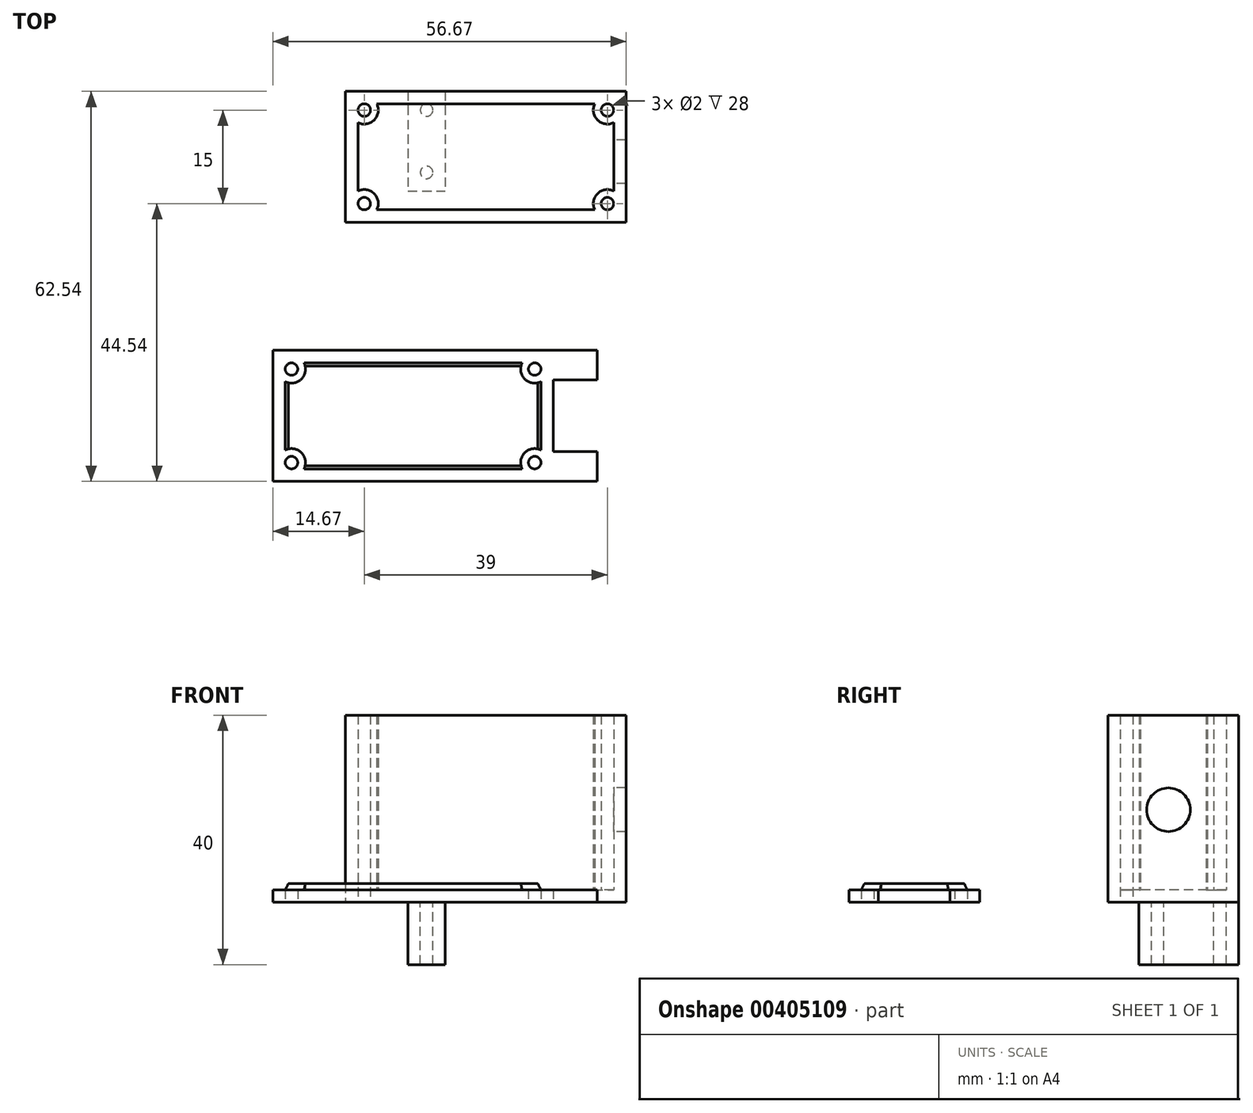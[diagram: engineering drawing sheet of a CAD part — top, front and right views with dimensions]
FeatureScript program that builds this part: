
annotation { "Feature Type Name" : "Feature", "Feature Type Description" : "" }
export const myFeature = defineFeature(function(context is Context, id is Id, definition is map)
    precondition{}
    {
        {
            var Q0;
            Q0=qCreatedBy(makeId("Top.planeOp"),FACE);
            var sketch = newSketch(context, id + "F0", { "sketchPlane" : qUnion([Q0])});
            skCircle(sketch, "E0", {"center": v(0, 0) * mm, "radius": 1 * mm});
            skCircle(sketch, "E1", {"center": v(0, -10) * mm, "radius": 1 * mm});
            skLineSegment(sketch, "E2.bottom", {"start": v(-3, 3) * mm, "end": v(3, 3) * mm});
            skLineSegment(sketch, "E2.top", {"start": v(-3, -13) * mm, "end": v(3, -13) * mm});
            skLineSegment(sketch, "E2.left", {"start": v(-3, 3) * mm, "end": v(-3, -13) * mm});
            skLineSegment(sketch, "E2.right", {"start": v(3, 3) * mm, "end": v(3, -13) * mm});
            skLineSegment(sketch, "E3.bottom", {"start": v(-13, 3) * mm, "end": v(32, 3) * mm});
            skLineSegment(sketch, "E3.top", {"start": v(-13, -18) * mm, "end": v(32, -18) * mm});
            skLineSegment(sketch, "E3.left", {"start": v(-13, 3) * mm, "end": v(-13, -18) * mm});
            skLineSegment(sketch, "E3.right", {"start": v(32, 3) * mm, "end": v(32, -18) * mm});
            skLineSegment(sketch, "E4.bottom", {"start": v(-11, 1) * mm, "end": v(30, 1) * mm});
            skLineSegment(sketch, "E4.top", {"start": v(-11, -16) * mm, "end": v(30, -16) * mm});
            skLineSegment(sketch, "E4.left", {"start": v(-11, 1) * mm, "end": v(-11, -16) * mm});
            skLineSegment(sketch, "E4.right", {"start": v(30, 1) * mm, "end": v(30, -16) * mm});
            skCircle(sketch, "E5", {"center": v(-10, 0) * mm, "radius": 1 * mm});
            skCircle(sketch, "E6", {"center": v(-10, -15) * mm, "radius": 1 * mm});
            skCircle(sketch, "E7", {"center": v(29, -15) * mm, "radius": 1 * mm});
            skCircle(sketch, "E8", {"center": v(29, 0) * mm, "radius": 1 * mm});
            skCircle(sketch, "E9", {"center": v(-10, 0) * mm, "radius": 2.25 * mm});
            skCircle(sketch, "E10", {"center": v(-10, -15) * mm, "radius": 2.25 * mm});
            skCircle(sketch, "E11", {"center": v(29, 0) * mm, "radius": 2.25 * mm});
            skCircle(sketch, "E12", {"center": v(29, -15) * mm, "radius": 2.25 * mm});
            skCircle(sketch, "E13", {"center": v(-11.67, -41.54) * mm, "radius": 1 * mm});
            skCircle(sketch, "E14", {"center": v(-11.67, -51.54) * mm, "radius": 1 * mm});
            skLineSegment(sketch, "E15.bottom", {"start": v(-14.67, -38.54) * mm, "end": v(-8.67, -38.54) * mm});
            skLineSegment(sketch, "E15.top", {"start": v(-14.67, -54.54) * mm, "end": v(-8.67, -54.54) * mm});
            skLineSegment(sketch, "E15.left", {"start": v(-14.67, -38.54) * mm, "end": v(-14.67, -54.54) * mm});
            skLineSegment(sketch, "E15.right", {"start": v(-8.67, -38.54) * mm, "end": v(-8.67, -54.54) * mm});
            skLineSegment(sketch, "E16.bottom", {"start": v(-24.67, -38.54) * mm, "end": v(20.33, -38.54) * mm});
            skLineSegment(sketch, "E16.top", {"start": v(-24.67, -59.54) * mm, "end": v(20.33, -59.54) * mm});
            skLineSegment(sketch, "E16.left", {"start": v(-24.67, -38.54) * mm, "end": v(-24.67, -59.54) * mm});
            skLineSegment(sketch, "E16.right", {"start": v(20.33, -38.54) * mm, "end": v(20.33, -59.54) * mm});
            skLineSegment(sketch, "E17.bottom", {"start": v(-22.67, -40.54) * mm, "end": v(18.33, -40.54) * mm});
            skLineSegment(sketch, "E17.top", {"start": v(-22.67, -57.54) * mm, "end": v(18.33, -57.54) * mm});
            skLineSegment(sketch, "E17.left", {"start": v(-22.67, -40.54) * mm, "end": v(-22.67, -57.54) * mm});
            skLineSegment(sketch, "E17.right", {"start": v(18.33, -40.54) * mm, "end": v(18.33, -57.54) * mm});
            skCircle(sketch, "E18", {"center": v(-21.67, -41.54) * mm, "radius": 1 * mm});
            skCircle(sketch, "E19", {"center": v(-21.67, -56.54) * mm, "radius": 1 * mm});
            skCircle(sketch, "E20", {"center": v(17.33, -56.54) * mm, "radius": 1 * mm});
            skCircle(sketch, "E21", {"center": v(17.33, -41.54) * mm, "radius": 1 * mm});
            skCircle(sketch, "E22", {"center": v(-21.67, -41.54) * mm, "radius": 2.25 * mm});
            skCircle(sketch, "E23", {"center": v(-21.67, -56.54) * mm, "radius": 2.25 * mm});
            skCircle(sketch, "E24", {"center": v(17.33, -41.54) * mm, "radius": 2.25 * mm});
            skCircle(sketch, "E25", {"center": v(17.33, -56.54) * mm, "radius": 2.25 * mm});
            skLineSegment(sketch, "E26.bottom", {"start": v(20.33, -38.54) * mm, "end": v(27.33, -38.54) * mm});
            skLineSegment(sketch, "E26.top", {"start": v(20.33, -59.54) * mm, "end": v(27.33, -59.54) * mm});
            skLineSegment(sketch, "E26.right", {"start": v(27.33, -38.54) * mm, "end": v(27.33, -59.54) * mm});
            skLineSegment(sketch, "E27", {"start": v(20.33, -54.8) * mm, "end": v(27.33, -54.8) * mm});
            skLineSegment(sketch, "E28", {"start": v(20.33, -43.3) * mm, "end": v(27.33, -43.3) * mm});
            skSolve(sketch);
        }
        {
            var Q0;
            {var subQ2=sQuery(id+"F0.wireOp",EDGE,"E2.left");var subQ4=sQuery(id+"F0.wireOp",EDGE,"E3.bottom");var subQ8=makeQuery(id+"F0.imprint","INTERSECT",VERTEX,{"derivedFrom":[subQ2,subQ4]});Q0=makeQuery(id+"F0.imprint","IMPRINT",FACE,{"disambiguationData":[TD([[makeQuery(id+"F0.imprint","IMPRINT",EDGE,{"disambiguationData":[TD([[subQ8,-1.0]])],"derivedFrom":subQ2}),1.0]])]});}
            var Q1;
            Q1=makeQuery(id+"F0.imprint","IMPRINT",FACE,{"disambiguationData":[TD([[makeQuery(id+"F0.imprint","IMPRINT",EDGE,{"derivedFrom":sQuery(id+"F0.wireOp",EDGE,"E3.top")}),1.0]])]});
            var Q2;
            {var subQ0=sQuery(id+"F0.wireOp",EDGE,"E5");var subQ1=sQuery(id+"F0.wireOp",EDGE,"E4.bottom");var subQ2=makeQuery(id+"F0.imprint","INTERSECT",VERTEX,{"derivedFrom":[subQ1,subQ0]});Q2=makeQuery(id+"F0.imprint","IMPRINT",FACE,{"disambiguationData":[TD([[makeQuery(id+"F0.imprint","IMPRINT",EDGE,{"disambiguationData":[TD([[subQ2,-1.0]])],"derivedFrom":subQ1}),-1.0]])]});}
            var Q3;
            {var subQ1=sQuery(id+"F0.wireOp",EDGE,"E4.left");var subQ5=sQuery(id+"F0.wireOp",EDGE,"E4.bottom");var subQ6=makeQuery(id+"F0.imprint","INTERSECT",VERTEX,{"derivedFrom":[subQ5,subQ1]});Q3=makeQuery(id+"F0.imprint","IMPRINT",FACE,{"disambiguationData":[TD([[makeQuery(id+"F0.imprint","IMPRINT",EDGE,{"disambiguationData":[TD([[subQ6,-1.0]])],"derivedFrom":subQ5}),1.0]])]});}
            var Q4;
            {var subQ3=sQuery(id+"F0.wireOp",EDGE,"E11");var subQ5=sQuery(id+"F0.wireOp",EDGE,"E4.bottom");var subQ8=makeQuery(id+"F0.imprint","INTERSECT",VERTEX,{"derivedFrom":[subQ5,subQ3]});Q4=makeQuery(id+"F0.imprint","IMPRINT",FACE,{"disambiguationData":[TD([[makeQuery(id+"F0.imprint","IMPRINT",EDGE,{"disambiguationData":[TD([[subQ8,-1.0]])],"derivedFrom":subQ5}),1.0]])]});}
            var Q5;
            {var subQ0=sQuery(id+"F0.wireOp",EDGE,"E11");var subQ1=sQuery(id+"F0.wireOp",EDGE,"E4.bottom");var subQ2=makeQuery(id+"F0.imprint","INTERSECT",VERTEX,{"derivedFrom":[subQ1,subQ0]});Q5=makeQuery(id+"F0.imprint","IMPRINT",FACE,{"disambiguationData":[TD([[makeQuery(id+"F0.imprint","IMPRINT",EDGE,{"disambiguationData":[TD([[subQ2,-1.0]])],"derivedFrom":subQ1}),-1.0]])]});}
            var Q6;
            {var subQ0=sQuery(id+"F0.wireOp",EDGE,"E4.right");var subQ1=sQuery(id+"F0.wireOp",EDGE,"E4.bottom");var subQ2=makeQuery(id+"F0.imprint","INTERSECT",VERTEX,{"derivedFrom":[subQ1,subQ0]});Q6=makeQuery(id+"F0.imprint","IMPRINT",FACE,{"disambiguationData":[TD([[makeQuery(id+"F0.imprint","IMPRINT",EDGE,{"disambiguationData":[TD([[subQ2,1.0]])],"derivedFrom":subQ1}),-1.0]])]});}
            var Q7;
            {var subQ0=sQuery(id+"F0.wireOp",EDGE,"E4.left");var subQ1=sQuery(id+"F0.wireOp",EDGE,"E4.bottom");var subQ2=makeQuery(id+"F0.imprint","INTERSECT",VERTEX,{"derivedFrom":[subQ1,subQ0]});Q7=makeQuery(id+"F0.imprint","IMPRINT",FACE,{"disambiguationData":[TD([[makeQuery(id+"F0.imprint","IMPRINT",EDGE,{"disambiguationData":[TD([[subQ2,-1.0]])],"derivedFrom":subQ1}),-1.0]])]});}
            var Q8;
            {var subQ0=sQuery(id+"F0.wireOp",EDGE,"E4.left");var subQ1=sQuery(id+"F0.wireOp",EDGE,"E4.top");var subQ2=makeQuery(id+"F0.imprint","INTERSECT",VERTEX,{"derivedFrom":[subQ1,subQ0]});Q8=makeQuery(id+"F0.imprint","IMPRINT",FACE,{"disambiguationData":[TD([[makeQuery(id+"F0.imprint","IMPRINT",EDGE,{"disambiguationData":[TD([[subQ2,-1.0]])],"derivedFrom":subQ1}),1.0]])]});}
            var Q9;
            {var subQ1=sQuery(id+"F0.wireOp",EDGE,"E4.left");var subQ5=sQuery(id+"F0.wireOp",EDGE,"E4.top");var subQ8=makeQuery(id+"F0.imprint","INTERSECT",VERTEX,{"derivedFrom":[subQ5,subQ1]});Q9=makeQuery(id+"F0.imprint","IMPRINT",FACE,{"disambiguationData":[TD([[makeQuery(id+"F0.imprint","IMPRINT",EDGE,{"disambiguationData":[TD([[subQ8,-1.0]])],"derivedFrom":subQ5}),-1.0]])]});}
            var Q10;
            {var subQ0=sQuery(id+"F0.wireOp",EDGE,"E6");var subQ1=sQuery(id+"F0.wireOp",EDGE,"E4.top");var subQ2=makeQuery(id+"F0.imprint","INTERSECT",VERTEX,{"derivedFrom":[subQ1,subQ0]});Q10=makeQuery(id+"F0.imprint","IMPRINT",FACE,{"disambiguationData":[TD([[makeQuery(id+"F0.imprint","IMPRINT",EDGE,{"disambiguationData":[TD([[subQ2,-1.0]])],"derivedFrom":subQ1}),1.0]])]});}
            var Q11;
            {var subQ0=sQuery(id+"F0.wireOp",EDGE,"E4.right");var subQ1=sQuery(id+"F0.wireOp",EDGE,"E4.top");var subQ2=makeQuery(id+"F0.imprint","INTERSECT",VERTEX,{"derivedFrom":[subQ1,subQ0]});Q11=makeQuery(id+"F0.imprint","IMPRINT",FACE,{"disambiguationData":[TD([[makeQuery(id+"F0.imprint","IMPRINT",EDGE,{"disambiguationData":[TD([[subQ2,1.0]])],"derivedFrom":subQ1}),1.0]])]});}
            var Q12;
            {var subQ0=sQuery(id+"F0.wireOp",EDGE,"E12");var subQ1=sQuery(id+"F0.wireOp",EDGE,"E4.top");var subQ2=makeQuery(id+"F0.imprint","INTERSECT",VERTEX,{"derivedFrom":[subQ1,subQ0]});Q12=makeQuery(id+"F0.imprint","IMPRINT",FACE,{"disambiguationData":[TD([[makeQuery(id+"F0.imprint","IMPRINT",EDGE,{"disambiguationData":[TD([[subQ2,-1.0]])],"derivedFrom":subQ1}),1.0]])]});}
            var Q13;
            {var subQ1=sQuery(id+"F0.wireOp",EDGE,"E4.top");var subQ6=sQuery(id+"F0.wireOp",EDGE,"E12");var subQ8=makeQuery(id+"F0.imprint","INTERSECT",VERTEX,{"derivedFrom":[subQ1,subQ6]});Q13=makeQuery(id+"F0.imprint","IMPRINT",FACE,{"disambiguationData":[TD([[makeQuery(id+"F0.imprint","IMPRINT",EDGE,{"disambiguationData":[TD([[subQ8,-1.0]])],"derivedFrom":subQ1}),-1.0]])]});}
            extrude(context, id + "F1", {"entities" : qUnion([Q0, Q1, Q2, Q3, Q4, Q5, Q6, Q7, Q8, Q9, Q10, Q11, Q12, Q13]), "depth" : 30 * mm});
        }
        {
            var Q0;
            {var subQ18=sQuery(id+"F0.wireOp",EDGE,"E2.top");Q0=makeQuery(id+"F0.imprint","IMPRINT",FACE,{"disambiguationData":[TD([[makeQuery(id+"F0.imprint","IMPRINT",EDGE,{"derivedFrom":subQ18}),-1.0]])]});}
            var Q1;
            Q1=makeQuery(id+"F0.imprint","IMPRINT",FACE,{"disambiguationData":[TD([[makeQuery(id+"F0.imprint","IMPRINT",EDGE,{"derivedFrom":sQuery(id+"F0.wireOp",EDGE,"E0")}),1.0]])]});
            var Q2;
            Q2=makeQuery(id+"F0.imprint","IMPRINT",FACE,{"disambiguationData":[TD([[makeQuery(id+"F0.imprint","IMPRINT",EDGE,{"derivedFrom":sQuery(id+"F0.wireOp",EDGE,"E1")}),1.0]])]});
            var Q3;
            {var subQ4=sQuery(id+"F0.wireOp",EDGE,"E0");Q3=makeQuery(id+"F0.imprint","IMPRINT",FACE,{"disambiguationData":[TD([[makeQuery(id+"F0.imprint","IMPRINT",EDGE,{"derivedFrom":subQ4}),-1.0]])]});}
            var Q4;
            {var subQ0=sQuery(id+"F0.wireOp",EDGE,"E6");var subQ1=sQuery(id+"F0.wireOp",EDGE,"E4.left");var subQ2=makeQuery(id+"F0.imprint","INTERSECT",VERTEX,{"disambiguationData":[OD(0.0)],"derivedFrom":[subQ1,subQ0]});Q4=makeQuery(id+"F0.imprint","IMPRINT",FACE,{"disambiguationData":[TD([[makeQuery(id+"F0.imprint","IMPRINT",EDGE,{"disambiguationData":[TD([[subQ2,-1.0]])],"derivedFrom":subQ1}),1.0]])]});}
            var Q5;
            {var subQ0=sQuery(id+"F0.wireOp",EDGE,"E5");var subQ1=makeQuery(id+"F0.imprint","INTERSECT",VERTEX,{"derivedFrom":[sQuery(id+"F0.wireOp",EDGE,"E4.bottom"),subQ0]});Q5=makeQuery(id+"F0.imprint","IMPRINT",FACE,{"disambiguationData":[TD([[makeQuery(id+"F0.imprint","IMPRINT",EDGE,{"disambiguationData":[TD([[subQ1,-1.0]])],"derivedFrom":subQ0}),1.0]])]});}
            var Q6;
            {var subQ0=sQuery(id+"F0.wireOp",EDGE,"E7");var subQ1=makeQuery(id+"F0.imprint","INTERSECT",VERTEX,{"derivedFrom":[sQuery(id+"F0.wireOp",EDGE,"E4.top"),subQ0]});Q6=makeQuery(id+"F0.imprint","IMPRINT",FACE,{"disambiguationData":[TD([[makeQuery(id+"F0.imprint","IMPRINT",EDGE,{"disambiguationData":[TD([[subQ1,1.0]])],"derivedFrom":subQ0}),1.0]])]});}
            var Q7;
            {var subQ0=sQuery(id+"F0.wireOp",EDGE,"E8");var subQ1=makeQuery(id+"F0.imprint","INTERSECT",VERTEX,{"derivedFrom":[sQuery(id+"F0.wireOp",EDGE,"E4.bottom"),subQ0]});Q7=makeQuery(id+"F0.imprint","IMPRINT",FACE,{"disambiguationData":[TD([[makeQuery(id+"F0.imprint","IMPRINT",EDGE,{"disambiguationData":[TD([[subQ1,1.0]])],"derivedFrom":subQ0}),1.0]])]});}
            extrude(context, id + "F2", {"entities" : qUnion([Q0, Q1, Q2, Q3, Q4, Q5, Q6, Q7]), "operationType" : NewBodyOperationType.ADD, "depth" : 2 * mm});
        }
        {
            var Q0;
            {var subQ4=sQuery(id+"F0.wireOp",EDGE,"E0");Q0=makeQuery(id+"F0.imprint","IMPRINT",FACE,{"disambiguationData":[TD([[makeQuery(id+"F0.imprint","IMPRINT",EDGE,{"derivedFrom":subQ4}),-1.0]])]});}
            var Q1;
            {var subQ2=sQuery(id+"F0.wireOp",EDGE,"E2.left");var subQ4=sQuery(id+"F0.wireOp",EDGE,"E3.bottom");var subQ8=makeQuery(id+"F0.imprint","INTERSECT",VERTEX,{"derivedFrom":[subQ2,subQ4]});Q1=makeQuery(id+"F0.imprint","IMPRINT",FACE,{"disambiguationData":[TD([[makeQuery(id+"F0.imprint","IMPRINT",EDGE,{"disambiguationData":[TD([[subQ8,-1.0]])],"derivedFrom":subQ2}),1.0]])]});}
            extrude(context, id + "F3", {"entities" : qUnion([Q0, Q1]), "operationType" : NewBodyOperationType.ADD, "oppositeDirection" : true, "depth" : 10 * mm});
        }
        {
            var Q0;
            Q0=makeQuery(id+"F0.imprint","IMPRINT",FACE,{"disambiguationData":[TD([[makeQuery(id+"F0.imprint","IMPRINT",EDGE,{"derivedFrom":sQuery(id+"F0.wireOp",EDGE,"E16.top")}),1.0]])]});
            var Q1;
            {var subQ2=sQuery(id+"F0.wireOp",EDGE,"E15.left");var subQ4=sQuery(id+"F0.wireOp",EDGE,"E16.bottom");var subQ8=makeQuery(id+"F0.imprint","INTERSECT",VERTEX,{"derivedFrom":[subQ2,subQ4]});Q1=makeQuery(id+"F0.imprint","IMPRINT",FACE,{"disambiguationData":[TD([[makeQuery(id+"F0.imprint","IMPRINT",EDGE,{"disambiguationData":[TD([[subQ8,-1.0]])],"derivedFrom":subQ2}),1.0]])]});}
            var Q2;
            {var subQ0=sQuery(id+"F0.wireOp",EDGE,"E18");var subQ1=sQuery(id+"F0.wireOp",EDGE,"E17.bottom");var subQ2=makeQuery(id+"F0.imprint","INTERSECT",VERTEX,{"derivedFrom":[subQ1,subQ0]});Q2=makeQuery(id+"F0.imprint","IMPRINT",FACE,{"disambiguationData":[TD([[makeQuery(id+"F0.imprint","IMPRINT",EDGE,{"disambiguationData":[TD([[subQ2,-1.0]])],"derivedFrom":subQ1}),-1.0]])]});}
            var Q3;
            {var subQ0=sQuery(id+"F0.wireOp",EDGE,"E19");var subQ1=sQuery(id+"F0.wireOp",EDGE,"E17.top");var subQ2=makeQuery(id+"F0.imprint","INTERSECT",VERTEX,{"derivedFrom":[subQ1,subQ0]});Q3=makeQuery(id+"F0.imprint","IMPRINT",FACE,{"disambiguationData":[TD([[makeQuery(id+"F0.imprint","IMPRINT",EDGE,{"disambiguationData":[TD([[subQ2,-1.0]])],"derivedFrom":subQ1}),1.0]])]});}
            var Q4;
            {var subQ3=sQuery(id+"F0.wireOp",EDGE,"E24");var subQ5=sQuery(id+"F0.wireOp",EDGE,"E17.bottom");var subQ8=makeQuery(id+"F0.imprint","INTERSECT",VERTEX,{"derivedFrom":[subQ5,subQ3]});Q4=makeQuery(id+"F0.imprint","IMPRINT",FACE,{"disambiguationData":[TD([[makeQuery(id+"F0.imprint","IMPRINT",EDGE,{"disambiguationData":[TD([[subQ8,-1.0]])],"derivedFrom":subQ5}),1.0]])]});}
            var Q5;
            {var subQ0=sQuery(id+"F0.wireOp",EDGE,"E24");var subQ1=sQuery(id+"F0.wireOp",EDGE,"E17.bottom");var subQ2=makeQuery(id+"F0.imprint","INTERSECT",VERTEX,{"derivedFrom":[subQ1,subQ0]});Q5=makeQuery(id+"F0.imprint","IMPRINT",FACE,{"disambiguationData":[TD([[makeQuery(id+"F0.imprint","IMPRINT",EDGE,{"disambiguationData":[TD([[subQ2,-1.0]])],"derivedFrom":subQ1}),-1.0]])]});}
            var Q6;
            {var subQ0=sQuery(id+"F0.wireOp",EDGE,"E25");var subQ1=sQuery(id+"F0.wireOp",EDGE,"E17.top");var subQ2=makeQuery(id+"F0.imprint","INTERSECT",VERTEX,{"derivedFrom":[subQ1,subQ0]});Q6=makeQuery(id+"F0.imprint","IMPRINT",FACE,{"disambiguationData":[TD([[makeQuery(id+"F0.imprint","IMPRINT",EDGE,{"disambiguationData":[TD([[subQ2,-1.0]])],"derivedFrom":subQ1}),1.0]])]});}
            var Q7;
            {var subQ0=sQuery(id+"F0.wireOp",EDGE,"E17.right");var subQ1=sQuery(id+"F0.wireOp",EDGE,"E17.top");var subQ2=makeQuery(id+"F0.imprint","INTERSECT",VERTEX,{"derivedFrom":[subQ1,subQ0]});Q7=makeQuery(id+"F0.imprint","IMPRINT",FACE,{"disambiguationData":[TD([[makeQuery(id+"F0.imprint","IMPRINT",EDGE,{"disambiguationData":[TD([[subQ2,1.0]])],"derivedFrom":subQ1}),1.0]])]});}
            var Q8;
            {var subQ1=sQuery(id+"F0.wireOp",EDGE,"E17.top");var subQ6=sQuery(id+"F0.wireOp",EDGE,"E25");var subQ8=makeQuery(id+"F0.imprint","INTERSECT",VERTEX,{"derivedFrom":[subQ1,subQ6]});Q8=makeQuery(id+"F0.imprint","IMPRINT",FACE,{"disambiguationData":[TD([[makeQuery(id+"F0.imprint","IMPRINT",EDGE,{"disambiguationData":[TD([[subQ8,-1.0]])],"derivedFrom":subQ1}),-1.0]])]});}
            var Q9;
            {var subQ1=sQuery(id+"F0.wireOp",EDGE,"E17.left");var subQ5=sQuery(id+"F0.wireOp",EDGE,"E17.top");var subQ8=makeQuery(id+"F0.imprint","INTERSECT",VERTEX,{"derivedFrom":[subQ5,subQ1]});Q9=makeQuery(id+"F0.imprint","IMPRINT",FACE,{"disambiguationData":[TD([[makeQuery(id+"F0.imprint","IMPRINT",EDGE,{"disambiguationData":[TD([[subQ8,-1.0]])],"derivedFrom":subQ5}),-1.0]])]});}
            var Q10;
            {var subQ1=sQuery(id+"F0.wireOp",EDGE,"E17.left");var subQ5=sQuery(id+"F0.wireOp",EDGE,"E17.bottom");var subQ6=makeQuery(id+"F0.imprint","INTERSECT",VERTEX,{"derivedFrom":[subQ5,subQ1]});Q10=makeQuery(id+"F0.imprint","IMPRINT",FACE,{"disambiguationData":[TD([[makeQuery(id+"F0.imprint","IMPRINT",EDGE,{"disambiguationData":[TD([[subQ6,-1.0]])],"derivedFrom":subQ5}),1.0]])]});}
            var Q11;
            {var subQ0=sQuery(id+"F0.wireOp",EDGE,"E17.left");var subQ1=sQuery(id+"F0.wireOp",EDGE,"E17.bottom");var subQ2=makeQuery(id+"F0.imprint","INTERSECT",VERTEX,{"derivedFrom":[subQ1,subQ0]});Q11=makeQuery(id+"F0.imprint","IMPRINT",FACE,{"disambiguationData":[TD([[makeQuery(id+"F0.imprint","IMPRINT",EDGE,{"disambiguationData":[TD([[subQ2,-1.0]])],"derivedFrom":subQ1}),-1.0]])]});}
            var Q12;
            {var subQ0=sQuery(id+"F0.wireOp",EDGE,"E17.left");var subQ1=sQuery(id+"F0.wireOp",EDGE,"E17.top");var subQ2=makeQuery(id+"F0.imprint","INTERSECT",VERTEX,{"derivedFrom":[subQ1,subQ0]});Q12=makeQuery(id+"F0.imprint","IMPRINT",FACE,{"disambiguationData":[TD([[makeQuery(id+"F0.imprint","IMPRINT",EDGE,{"disambiguationData":[TD([[subQ2,-1.0]])],"derivedFrom":subQ1}),1.0]])]});}
            var Q13;
            {var subQ0=sQuery(id+"F0.wireOp",EDGE,"E17.right");var subQ1=sQuery(id+"F0.wireOp",EDGE,"E17.bottom");var subQ2=makeQuery(id+"F0.imprint","INTERSECT",VERTEX,{"derivedFrom":[subQ1,subQ0]});Q13=makeQuery(id+"F0.imprint","IMPRINT",FACE,{"disambiguationData":[TD([[makeQuery(id+"F0.imprint","IMPRINT",EDGE,{"disambiguationData":[TD([[subQ2,1.0]])],"derivedFrom":subQ1}),-1.0]])]});}
            extrude(context, id + "F4", {"entities" : qUnion([Q0, Q1, Q2, Q3, Q4, Q5, Q6, Q7, Q8, Q9, Q10, Q11, Q12, Q13]), "depth" : 2 * mm});
        }
        {
            var Q0;
            {var subQ18=sQuery(id+"F0.wireOp",EDGE,"E15.top");Q0=makeQuery(id+"F0.imprint","IMPRINT",FACE,{"disambiguationData":[TD([[makeQuery(id+"F0.imprint","IMPRINT",EDGE,{"derivedFrom":subQ18}),-1.0]])]});}
            var Q1;
            Q1=makeQuery(id+"F0.imprint","IMPRINT",FACE,{"disambiguationData":[TD([[makeQuery(id+"F0.imprint","IMPRINT",EDGE,{"derivedFrom":sQuery(id+"F0.wireOp",EDGE,"E13")}),1.0]])]});
            var Q2;
            Q2=makeQuery(id+"F0.imprint","IMPRINT",FACE,{"disambiguationData":[TD([[makeQuery(id+"F0.imprint","IMPRINT",EDGE,{"derivedFrom":sQuery(id+"F0.wireOp",EDGE,"E14")}),1.0]])]});
            var Q3;
            {var subQ4=sQuery(id+"F0.wireOp",EDGE,"E13");Q3=makeQuery(id+"F0.imprint","IMPRINT",FACE,{"disambiguationData":[TD([[makeQuery(id+"F0.imprint","IMPRINT",EDGE,{"derivedFrom":subQ4}),-1.0]])]});}
            extrude(context, id + "F5", {"entities" : qUnion([Q0, Q1, Q2, Q3]), "operationType" : NewBodyOperationType.ADD, "depth" : 3 * mm});
        }
        {
            var Q0;
            Q0=makeQuery(id+"F5.opExtrude","CAP_EDGE",EDGE,{"disambiguationData":[OSD([sQuery(id+"F0.wireOp",EDGE,"E17.top")])],"isStart":false});
            var Q1;
            Q1=makeQuery(id+"F5.opExtrude","CAP_EDGE",EDGE,{"disambiguationData":[OSD([sQuery(id+"F0.wireOp",EDGE,"E17.left")])],"isStart":false});
            var Q2;
            Q2=makeQuery(id+"F5.opExtrude","CAP_EDGE",EDGE,{"disambiguationData":[OSD([sQuery(id+"F0.wireOp",EDGE,"E17.bottom")])],"isStart":false});
            var Q3;
            Q3=makeQuery(id+"F5.opExtrude","CAP_EDGE",EDGE,{"disambiguationData":[OSD([sQuery(id+"F0.wireOp",EDGE,"E17.right")])],"isStart":false});
            chamfer(context, id + "F6", {"entities" : qUnion([Q0, Q1, Q2, Q3]), "chamferType" : ChamferType.TWO_OFFSETS, "width1" : .5 * mm, "oppositeDirection" : false, "width2" : 1 * mm, "tangentPropagation" : true});
        }
        {
            var Q0;
            Q0=qCreatedBy(makeId("Right.planeOp"),FACE);
            var sketch = newSketch(context, id + "F7", { "sketchPlane" : qUnion([Q0])});
            skCircle(sketch, "E29", {"center": v(-8.29, 14.83) * mm, "radius": 3.5 * mm});
            skSolve(sketch);
        }
        {
            var Q0;
            Q0 = qSketchRegion(id + "F7", true);
            extrude(context, id + "F8", {"entities" : qUnion([Q0]), "operationType" : NewBodyOperationType.REMOVE, "depth" : 40 * mm});
        }
        {
            var Q0;
            {var subQ0=sQuery(id+"F0.wireOp",EDGE,"E26.bottom");Q0=makeQuery(id+"F0.imprint","IMPRINT",FACE,{"disambiguationData":[TD([[makeQuery(id+"F0.imprint","IMPRINT",EDGE,{"derivedFrom":subQ0}),-1.0]])]});}
            var Q1;
            {var subQ0=sQuery(id+"F0.wireOp",EDGE,"E26.top");Q1=makeQuery(id+"F0.imprint","IMPRINT",FACE,{"disambiguationData":[TD([[makeQuery(id+"F0.imprint","IMPRINT",EDGE,{"derivedFrom":subQ0}),1.0]])]});}
            extrude(context, id + "F9", {"entities" : qUnion([Q0, Q1]), "operationType" : NewBodyOperationType.ADD, "depth" : 2 * mm});
        }
    });
